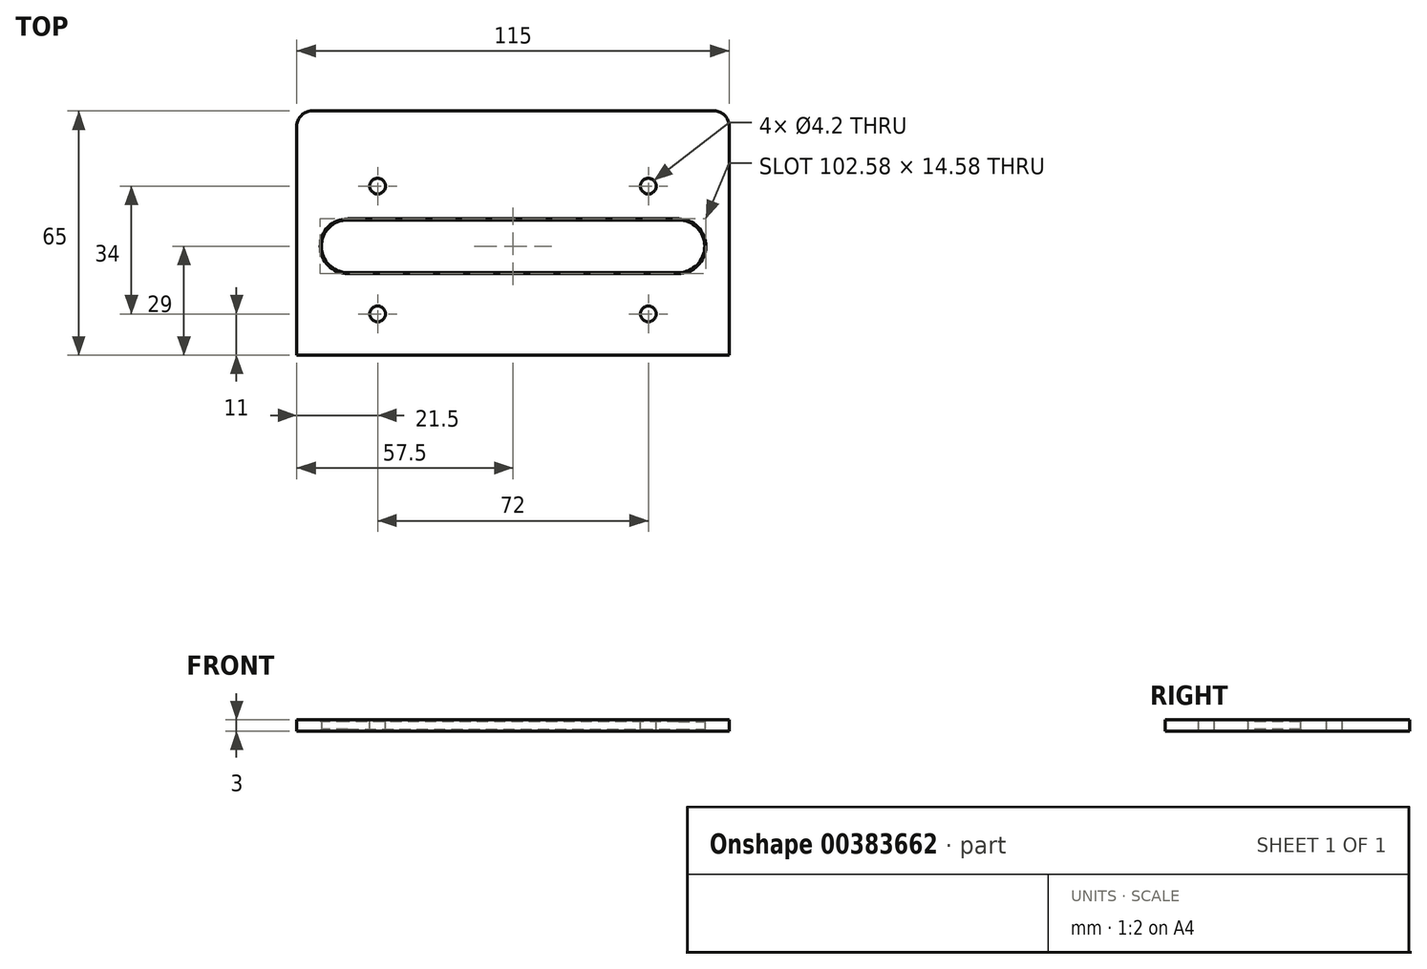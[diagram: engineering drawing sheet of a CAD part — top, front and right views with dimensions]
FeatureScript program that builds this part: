
annotation { "Feature Type Name" : "Feature", "Feature Type Description" : "" }
export const myFeature = defineFeature(function(context is Context, id is Id, definition is map)
    precondition{}
    {
        {
            var Q0;
            Q0=qCreatedBy(makeId("Top.planeOp"),FACE);
            var sketch = newSketch(context, id + "F0", { "sketchPlane" : qUnion([Q0])});
            skLineSegment(sketch, "E0.bottom", {"start": v(-57.5, 32.5) * mm, "end": v(57.5, 32.5) * mm});
            skLineSegment(sketch, "E0.top", {"start": v(-57.5, -32.5) * mm, "end": v(57.5, -32.5) * mm});
            skLineSegment(sketch, "E0.left", {"start": v(-57.5, 32.5) * mm, "end": v(-57.5, -32.5) * mm});
            skLineSegment(sketch, "E0.right", {"start": v(57.5, 32.5) * mm, "end": v(57.5, -32.5) * mm});
            skPoint(sketch, "E0.middle", {"position": v(0, 0) * mm});
            skLineSegment(sketch, "E1.bottom", {"start": v(-44, -10.5) * mm, "end": v(44, -10.5) * mm});
            skLineSegment(sketch, "E1.top", {"start": v(-44, 3.5) * mm, "end": v(44, 3.5) * mm});
            skArc(sketch, "E2", {"start": v(-44, 3.5) * mm, "mid": v(-51, -3.5) * mm, "end": v(-44, -10.5) * mm});
            skArc(sketch, "E3", {"start": v(44, -10.5) * mm, "mid": v(51, -3.5) * mm, "end": v(44, 3.5) * mm});
            skLineSegment(sketch, "E4", {"start": v(0, 3.5) * mm, "end": v(0, -10.5) * mm, "construction": true});
            skSolve(sketch);
        }
        {
            var Q0;
            Q0=makeQuery(id+"F0.imprint","IMPRINT",FACE,{"disambiguationData":[TD([[makeQuery(id+"F0.imprint","IMPRINT",EDGE,{"derivedFrom":sQuery(id+"F0.wireOp",EDGE,"E0.bottom")}),-1.0]])]});
            extrude(context, id + "F1", {"entities" : qUnion([Q0]), "depth" : 3 * mm});
        }
        {
            var Q0;
            Q0=makeQuery(id+"F1.opExtrude","CAP_FACE",FACE,{"disambiguationData":[OSD([sQuery(id+"F0.wireOp",EDGE,"E0.bottom"),sQuery(id+"F0.wireOp",EDGE,"E0.top"),sQuery(id+"F0.wireOp",EDGE,"E0.left"),sQuery(id+"F0.wireOp",EDGE,"E0.right"),sQuery(id+"F0.wireOp",EDGE,"E1.bottom"),sQuery(id+"F0.wireOp",EDGE,"E1.top"),sQuery(id+"F0.wireOp",EDGE,"E2"),sQuery(id+"F0.wireOp",EDGE,"E3")])],"isStart":false});
            var sketch = newSketch(context, id + "F2", { "sketchPlane" : qUnion([Q0])});
            skCircle(sketch, "E5", {"center": v(-36, -21.5) * mm, "radius": 2.1 * mm});
            skCircle(sketch, "E6", {"center": v(36, -21.5) * mm, "radius": 2.1 * mm});
            skCircle(sketch, "E7", {"center": v(36, 12.5) * mm, "radius": 2.1 * mm});
            skCircle(sketch, "E8", {"center": v(-36, 12.5) * mm, "radius": 2.1 * mm});
            skSolve(sketch);
        }
        {
            var Q0;
            Q0=makeQuery(id+"F2.imprint","IMPRINT",FACE,{"disambiguationData":[TD([[makeQuery(id+"F2.imprint","IMPRINT",EDGE,{"derivedFrom":sQuery(id+"F2.wireOp",EDGE,"E5")}),1.0]])]});
            var Q1;
            Q1=makeQuery(id+"F2.imprint","IMPRINT",FACE,{"disambiguationData":[TD([[makeQuery(id+"F2.imprint","IMPRINT",EDGE,{"derivedFrom":sQuery(id+"F2.wireOp",EDGE,"E6")}),1.0]])]});
            var Q2;
            Q2=makeQuery(id+"F2.imprint","IMPRINT",FACE,{"disambiguationData":[TD([[makeQuery(id+"F2.imprint","IMPRINT",EDGE,{"derivedFrom":sQuery(id+"F2.wireOp",EDGE,"E7")}),1.0]])]});
            var Q3;
            Q3=makeQuery(id+"F2.imprint","IMPRINT",FACE,{"disambiguationData":[TD([[makeQuery(id+"F2.imprint","IMPRINT",EDGE,{"derivedFrom":sQuery(id+"F2.wireOp",EDGE,"E8")}),1.0]])]});
            extrude(context, id + "F3", {"entities" : qUnion([Q0, Q1, Q2, Q3]), "operationType" : NewBodyOperationType.REMOVE, "oppositeDirection" : true, "depth" : 25 * mm});
        }
        {
            var Q0;
            Q0=makeQuery(id+"F1.opExtrude","SWEPT_EDGE",EDGE,{"disambiguationData":[OSD([sQuery(id+"F0.wireOp",EDGE,"E0.bottom"),sQuery(id+"F0.wireOp",EDGE,"E0.right")])]});
            var Q1;
            Q1=makeQuery(id+"F1.opExtrude","SWEPT_EDGE",EDGE,{"disambiguationData":[OSD([sQuery(id+"F0.wireOp",EDGE,"E0.bottom"),sQuery(id+"F0.wireOp",EDGE,"E0.left")])]});
            fillet(context, id + "F4", {"entities" : qUnion([Q0, Q1]), "radius" : 4 * mm, "tangentPropagation" : true, "allowEdgeOverflow" : false});
        }
        {
            var Q0;
            Q0=makeQuery(id+"F1.opExtrude","CAP_EDGE",EDGE,{"disambiguationData":[OSD([sQuery(id+"F0.wireOp",EDGE,"E1.top")])],"isStart":false});
            var Q1;
            Q1=makeQuery(id+"F1.opExtrude","CAP_EDGE",EDGE,{"disambiguationData":[OSD([sQuery(id+"F0.wireOp",EDGE,"E1.top")])],"isStart":true});
            chamfer(context, id + "F5", {"entities" : qUnion([Q0, Q1]), "chamferType" : ChamferType.OFFSET_ANGLE, "width" : 0.5 * mm, "oppositeDirection" : true, "angle" : 30 * degree, "tangentPropagation" : true});
        }
    });
